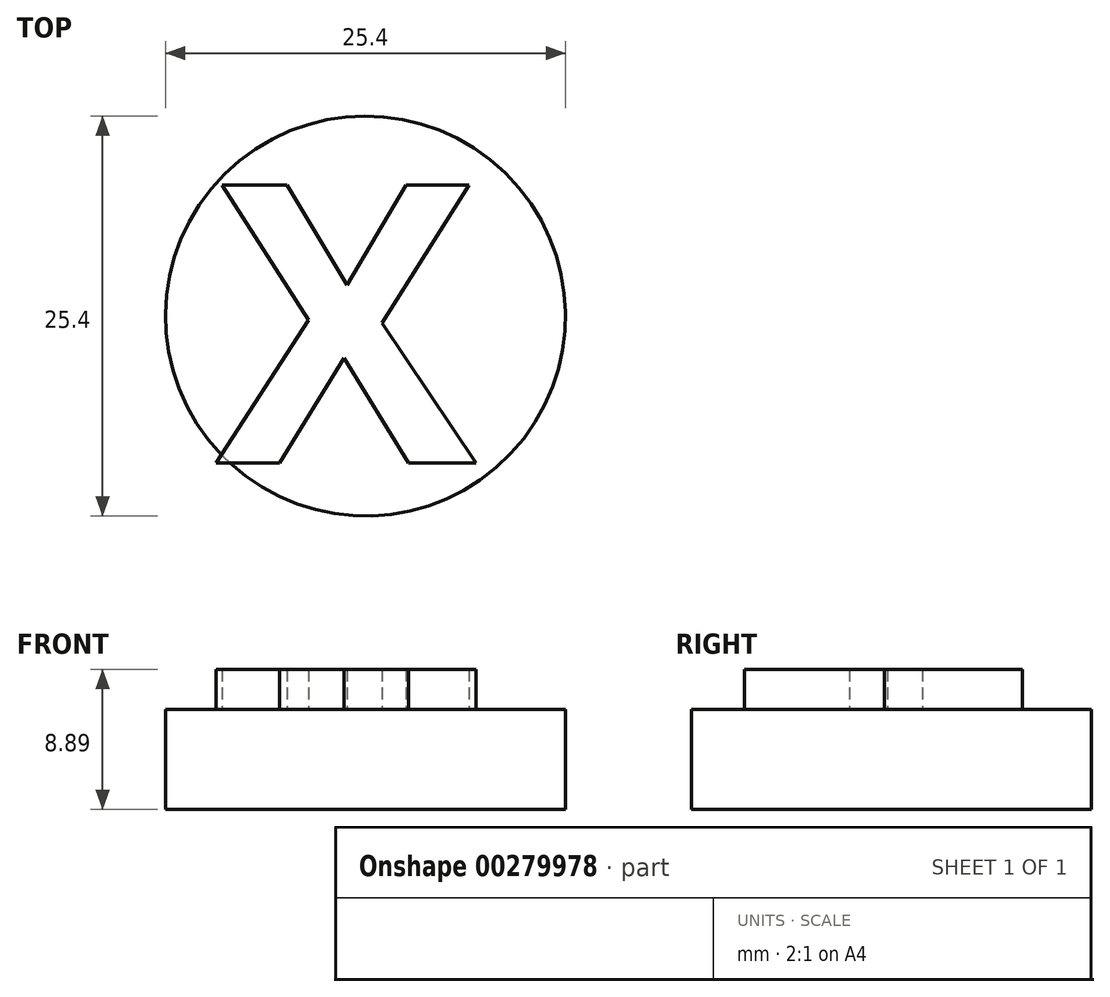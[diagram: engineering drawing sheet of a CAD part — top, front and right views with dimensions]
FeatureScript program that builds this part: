
annotation { "Feature Type Name" : "Feature", "Feature Type Description" : "" }
export const myFeature = defineFeature(function(context is Context, id is Id, definition is map)
    precondition{}
    {
        {
            var Q0;
            Q0=qCreatedBy(makeId("Top.planeOp"),FACE);
            var sketch = newSketch(context, id + "F0", { "sketchPlane" : qUnion([Q0])});
            skCircle(sketch, "E0", {"center": v(0, 0) * mm, "radius": 12.7 * mm});
            skSolve(sketch);
        }
        {
            var Q0;
            Q0=makeQuery(id+"F0.imprint","IMPRINT",FACE,{"disambiguationData":[TD([[makeQuery(id+"F0.imprint","IMPRINT",EDGE,{"derivedFrom":sQuery(id+"F0.wireOp",EDGE,"E0")}),1.0]])]});
            extrude(context, id + "F1", {"entities" : qUnion([Q0]), "depth" : 6.35 * mm});
        }
        {
            var Q0;
            Q0=makeQuery(id+"F1.opExtrude","CAP_FACE",FACE,{"disambiguationData":[OSD([sQuery(id+"F0.wireOp",EDGE,"E0")])],"isStart":false});
            var sketch = newSketch(context, id + "F2", { "sketchPlane" : qUnion([Q0])});
            skText(sketch, "E1", { "text": "X", "fontName": "OpenSans-Bold.ttf"});
            const initialGuessF2  = {"E1": [-0.00948, -0.00934, 1, 0, 0.0178]};
            skSetInitialGuess(sketch, initialGuessF2);
            skSolve(sketch);
        }
        {
            var Q0;
            Q0 = qSketchRegion(id + "F2", true);
            extrude(context, id + "F3", {"entities" : qUnion([Q0]), "operationType" : NewBodyOperationType.ADD, "depth" : 2.54 * mm});
        }
    });
